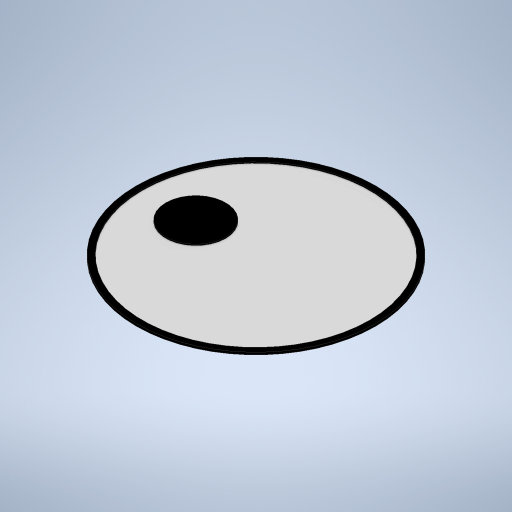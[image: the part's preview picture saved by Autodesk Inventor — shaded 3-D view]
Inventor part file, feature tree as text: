
AUTODESK INVENTOR PART (.ipt)
format: ipt  version: 2023 (Build 270158000, 158)  size: 240,640 bytes
history: native  units: mm
features: extrude x2, sketch x2, other x1, projected_geometry x1
ambient origin geometry x8: Origin, YZ Plane, XZ Plane, XY Plane, X Axis, Y Axis, Z Axis, Center Point
bodies: Body1 (feature_tree)
feature tree (6):
  other  "Bryła1"
  extrude  "Wyciągnięcie proste1"  Depth=20.0mm
  extrude  "Wyciągnięcie proste2"  Depth=0.1mm TaperAngle=0.0deg
  sketch  "Szkic1"
  sketch  "Szkic2"
  projected_geometry  "Pętla rzutowana1"
